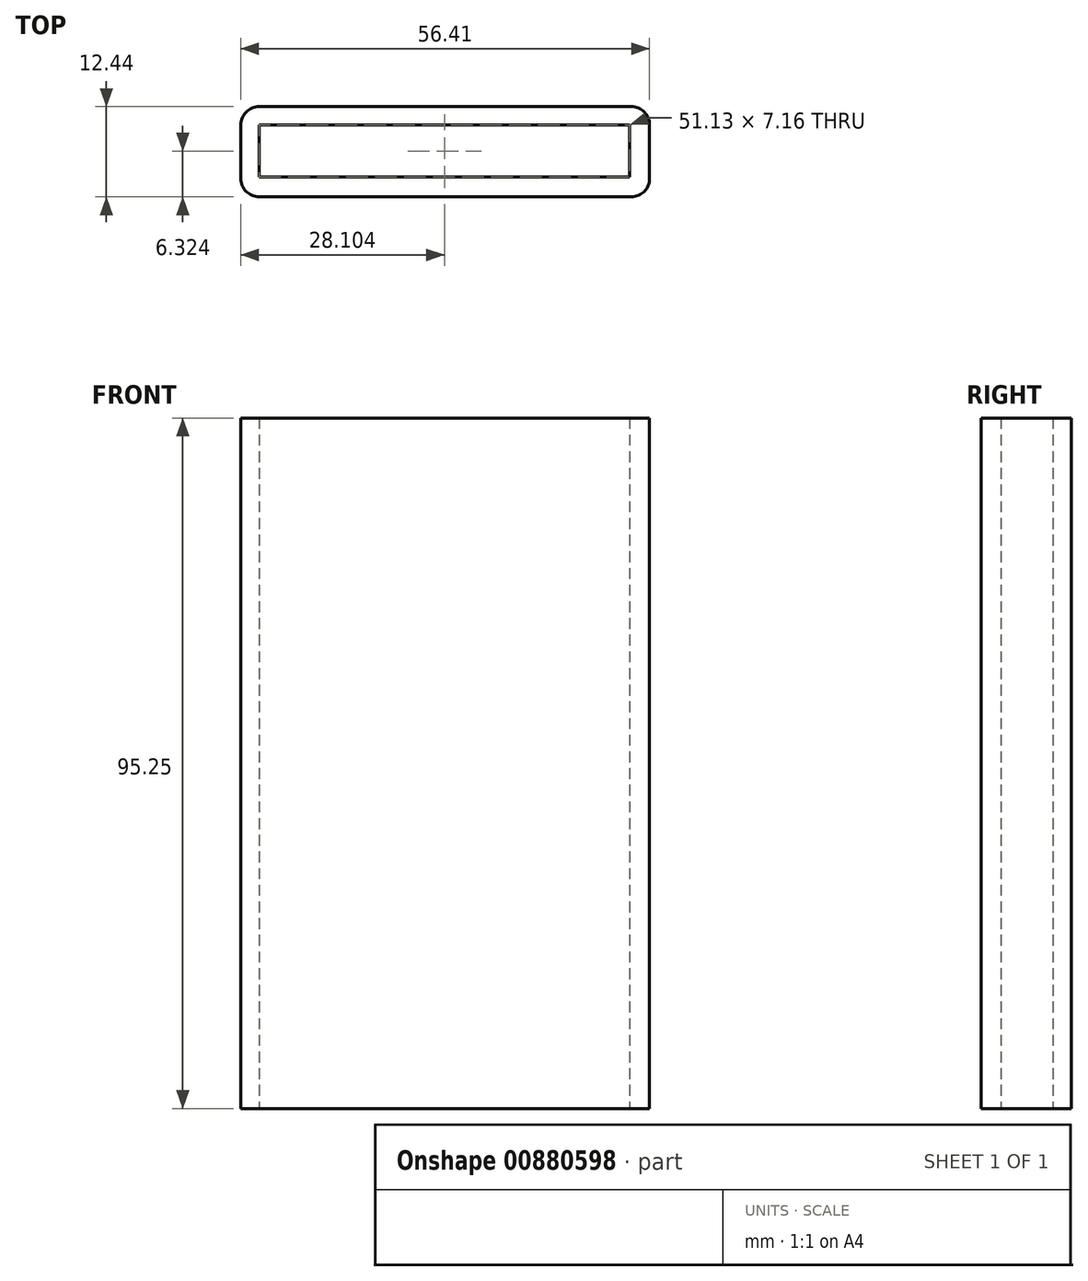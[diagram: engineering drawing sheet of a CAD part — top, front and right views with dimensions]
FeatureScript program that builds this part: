
annotation { "Feature Type Name" : "Feature", "Feature Type Description" : "" }
export const myFeature = defineFeature(function(context is Context, id is Id, definition is map)
    precondition{}
    {
        {
            var Q0;
            Q0=qCreatedBy(makeId("Top.planeOp"),FACE);
            var sketch = newSketch(context, id + "F0", { "sketchPlane" : qUnion([Q0])});
            skLineSegment(sketch, "E0.bottom", {"start": v(2.54, 0) * mm, "end": v(53.87, 0) * mm});
            skLineSegment(sketch, "E0.top", {"start": v(2.54, 12.44) * mm, "end": v(53.87, 12.44) * mm});
            skLineSegment(sketch, "E0.left", {"start": v(0, 2.54) * mm, "end": v(0, 9.9) * mm});
            skLineSegment(sketch, "E0.right", {"start": v(56.41, 2.54) * mm, "end": v(56.41, 9.9) * mm});
            skLineSegment(sketch, "E1.0", {"start": v(2.54, 0) * mm, "end": v(2.54, 12.44) * mm});
            skLineSegment(sketch, "E2.0", {"start": v(0, 9.9) * mm, "end": v(56.41, 9.9) * mm});
            skLineSegment(sketch, "E3.0", {"start": v(53.67, 2.74) * mm, "end": v(53.67, 12.44) * mm});
            skLineSegment(sketch, "E3.1", {"start": v(0, 2.74) * mm, "end": v(53.67, 2.74) * mm});
            skPoint(sketch, "E4.visualSharp", {"position": v(0, 12.44) * mm});
            skArc(sketch, "E4.filletArc", {"start": v(2.54, 12.44) * mm, "mid": v(0.74, 11.7) * mm, "end": v(0, 9.9) * mm});
            skPoint(sketch, "E5.visualSharp", {"position": v(0, 0) * mm});
            skArc(sketch, "E5.filletArc", {"start": v(0, 2.54) * mm, "mid": v(0.74, 0.74) * mm, "end": v(2.54, 0) * mm});
            skPoint(sketch, "E6.visualSharp", {"position": v(56.41, 0) * mm});
            skArc(sketch, "E6.filletArc", {"start": v(53.87, 0) * mm, "mid": v(55.67, 0.74) * mm, "end": v(56.41, 2.54) * mm});
            skPoint(sketch, "E7.visualSharp", {"position": v(56.41, 12.44) * mm});
            skArc(sketch, "E7.filletArc", {"start": v(56.41, 9.9) * mm, "mid": v(55.67, 11.7) * mm, "end": v(53.87, 12.44) * mm});
            skSolve(sketch);
        }
        {
            var Q0;
            {var subQ3=sQuery(id+"F0.wireOp",EDGE,"E3.1");var subQ5=sQuery(id+"F0.wireOp",EDGE,"E1.0");var subQ7=makeQuery(id+"F0.imprint","INTERSECT",VERTEX,{"derivedFrom":[subQ5,subQ3]});Q0=makeQuery(id+"F0.imprint","IMPRINT",FACE,{"disambiguationData":[TD([[makeQuery(id+"F0.imprint","IMPRINT",EDGE,{"disambiguationData":[TD([[subQ7,-1.0]])],"derivedFrom":subQ5}),1.0]])]});}
            var Q1;
            {var subQ0=sQuery(id+"F0.wireOp",EDGE,"E4.filletArc");Q1=makeQuery(id+"F0.imprint","IMPRINT",FACE,{"disambiguationData":[TD([[makeQuery(id+"F0.imprint","IMPRINT",EDGE,{"derivedFrom":subQ0}),1.0]])]});}
            var Q2;
            {var subQ0=sQuery(id+"F0.wireOp",EDGE,"E1.0");var subQ5=sQuery(id+"F0.wireOp",EDGE,"E2.0");var subQ6=makeQuery(id+"F0.imprint","INTERSECT",VERTEX,{"derivedFrom":[subQ0,subQ5]});Q2=makeQuery(id+"F0.imprint","IMPRINT",FACE,{"disambiguationData":[TD([[makeQuery(id+"F0.imprint","IMPRINT",EDGE,{"disambiguationData":[TD([[subQ6,-1.0]])],"derivedFrom":subQ5}),1.0]])]});}
            var Q3;
            {var subQ0=sQuery(id+"F0.wireOp",EDGE,"E7.filletArc");Q3=makeQuery(id+"F0.imprint","IMPRINT",FACE,{"disambiguationData":[TD([[makeQuery(id+"F0.imprint","IMPRINT",EDGE,{"derivedFrom":subQ0}),1.0]])]});}
            var Q4;
            {var subQ4=sQuery(id+"F0.wireOp",EDGE,"E0.bottom");Q4=makeQuery(id+"F0.imprint","IMPRINT",FACE,{"disambiguationData":[TD([[makeQuery(id+"F0.imprint","IMPRINT",EDGE,{"derivedFrom":subQ4}),1.0]])]});}
            var Q5;
            {var subQ0=sQuery(id+"F0.wireOp",EDGE,"E5.filletArc");Q5=makeQuery(id+"F0.imprint","IMPRINT",FACE,{"disambiguationData":[TD([[makeQuery(id+"F0.imprint","IMPRINT",EDGE,{"derivedFrom":subQ0}),1.0]])]});}
            extrude(context, id + "F1", {"entities" : qUnion([Q0, Q1, Q2, Q3, Q4, Q5]), "depth" : 95.25 * mm, "offsetDistance" : 25.4 * mm});
        }
    });
